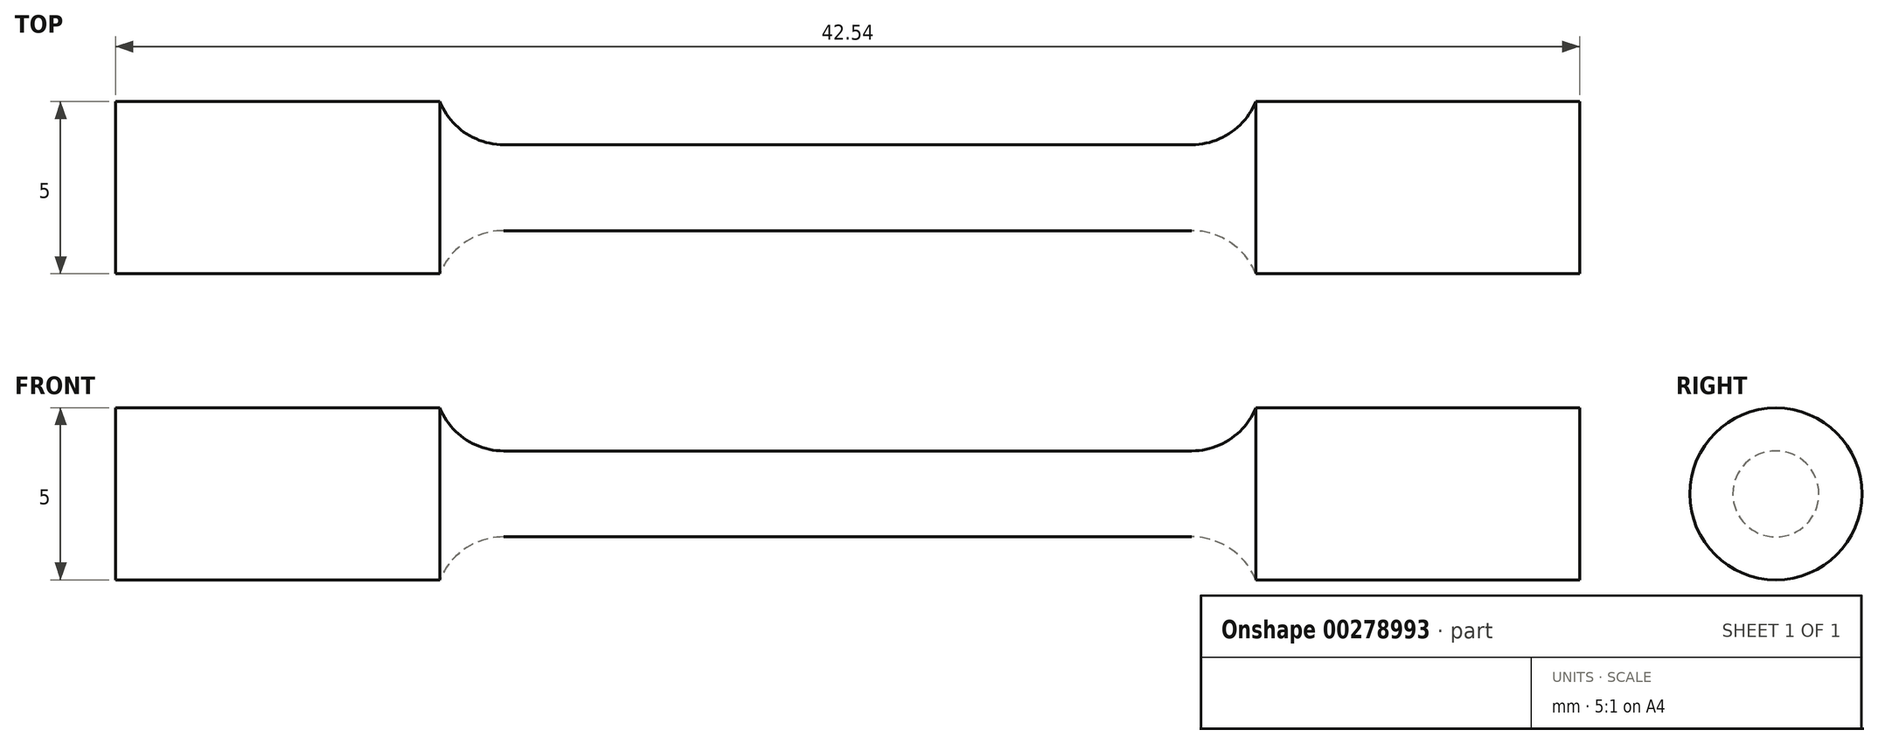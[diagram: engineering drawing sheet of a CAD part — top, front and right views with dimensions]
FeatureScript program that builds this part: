
annotation { "Feature Type Name" : "Feature", "Feature Type Description" : "" }
export const myFeature = defineFeature(function(context is Context, id is Id, definition is map)
    precondition{}
    {
        {
            var Q0;
            Q0=qCreatedBy(makeId("Front.planeOp"),FACE);
            var sketch = newSketch(context, id + "F0", { "sketchPlane" : qUnion([Q0])});
            skLineSegment(sketch, "E0", {"start": v(0, 1.25) * mm, "end": v(10, 1.25) * mm});
            skArc(sketch, "E1", {"start": v(10, 1.25) * mm, "mid": v(11.12, 1.6) * mm, "end": v(11.85, 2.5) * mm});
            skLineSegment(sketch, "E2", {"start": v(11.85, 2.5) * mm, "end": v(21.27, 2.5) * mm});
            skLineSegment(sketch, "E3", {"start": v(21.27, 2.5) * mm, "end": v(21.27, 0) * mm});
            skLineSegment(sketch, "E4.MirrorCS", {"start": v(0, 1.25) * mm, "end": v(-10, 1.25) * mm});
            skLineSegment(sketch, "E5.MirrorCS", {"start": v(-21.27, 2.5) * mm, "end": v(-21.27, 0) * mm});
            skLineSegment(sketch, "E6.MirrorCS", {"start": v(-11.85, 2.5) * mm, "end": v(-21.27, 2.5) * mm});
            skArc(sketch, "E7.MirrorCS", {"start": v(-10, 1.25) * mm, "mid": v(-11.12, 1.6) * mm, "end": v(-11.85, 2.5) * mm});
            skLineSegment(sketch, "E8", {"start": v(-21.27, 0) * mm, "end": v(21.27, 0) * mm});
            skSolve(sketch);
        }
        {
            var Q0;
            Q0 = qSketchRegion(id + "F0", true);
            var Q1;
            Q1=sQuery(id+"F0.wireOp",EDGE,"E8");
            revolve(context, id + "F1", {"entities" : qUnion([Q0]), "axis" : qUnion([Q1]), "revolveType" : RevolveType.FULL});
        }
    });
